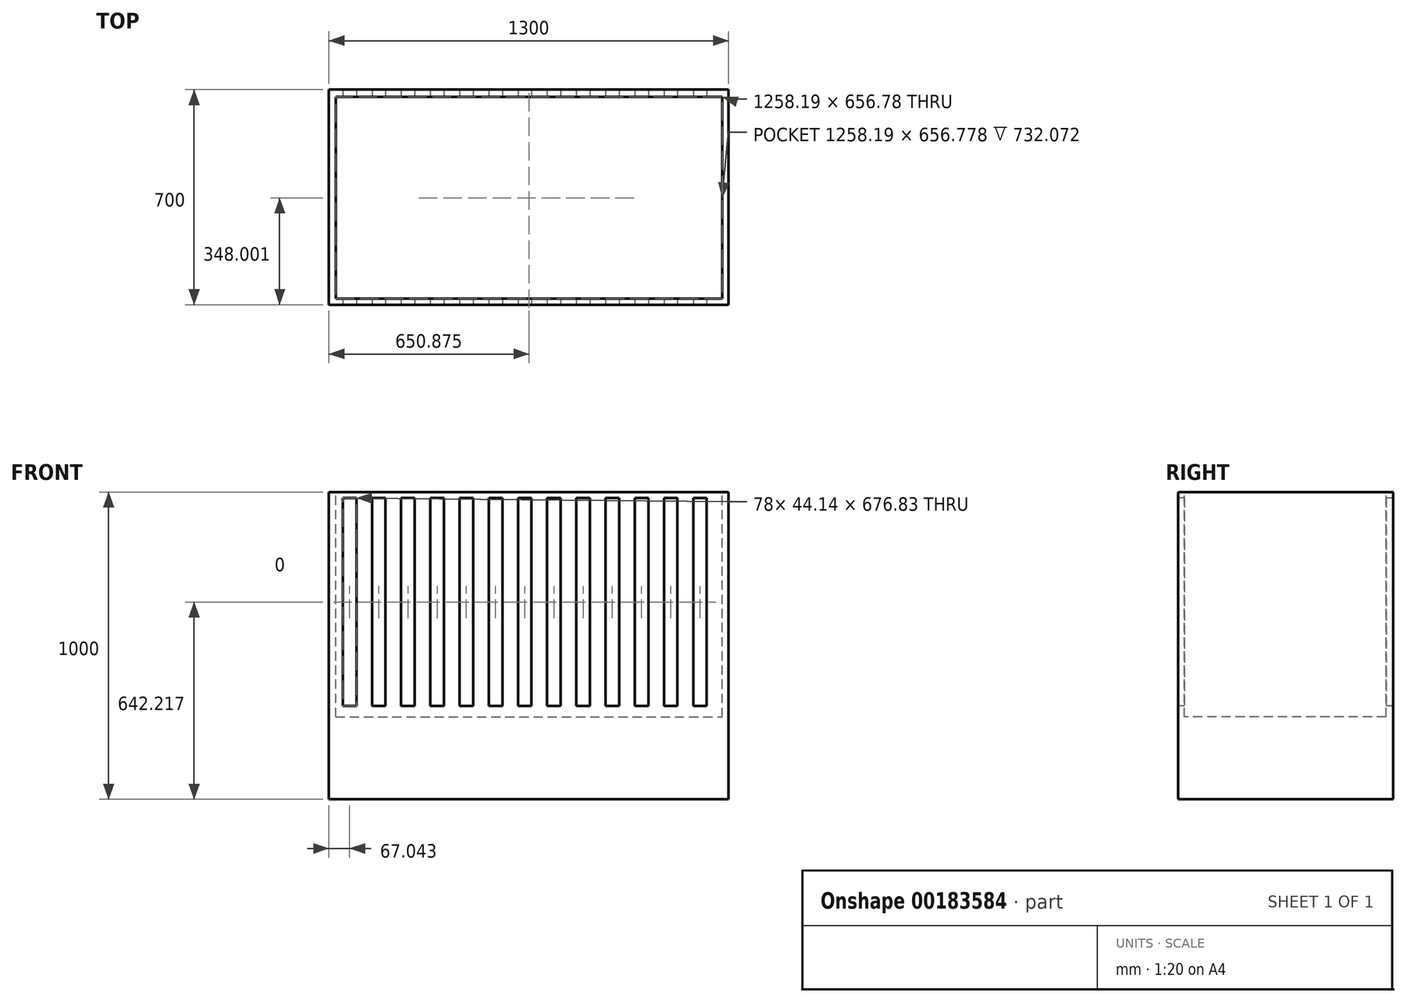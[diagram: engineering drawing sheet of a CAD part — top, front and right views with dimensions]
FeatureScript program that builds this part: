
annotation { "Feature Type Name" : "Feature", "Feature Type Description" : "" }
export const myFeature = defineFeature(function(context is Context, id is Id, definition is map)
    precondition{}
    {
        {
            var Q0;
            Q0=qCreatedBy(makeId("Top.planeOp"),FACE);
            var sketch = newSketch(context, id + "F0", { "sketchPlane" : qUnion([Q0])});
            skLineSegment(sketch, "E0.bottom", {"start": v(0, 0) * mm, "end": v(1300, 0) * mm});
            skLineSegment(sketch, "E0.top", {"start": v(0, 700) * mm, "end": v(1300, 700) * mm});
            skLineSegment(sketch, "E0.left", {"start": v(0, 0) * mm, "end": v(0, 700) * mm});
            skLineSegment(sketch, "E0.right", {"start": v(1300, 0) * mm, "end": v(1300, 700) * mm});
            skSolve(sketch);
        }
        {
            var Q0;
            Q0=makeQuery(id+"F0.imprint","IMPRINT",FACE,{"disambiguationData":[TD([[makeQuery(id+"F0.imprint","IMPRINT",EDGE,{"derivedFrom":sQuery(id+"F0.wireOp",EDGE,"E0.bottom")}),1.0]])]});
            extrude(context, id + "F1", {"entities" : qUnion([Q0]), "depth" : 1000 * mm});
        }
        {
            var Q0;
            Q0=makeQuery(id+"F1.opExtrude","CAP_FACE",FACE,{"disambiguationData":[OSD([sQuery(id+"F0.wireOp",EDGE,"E0.bottom"),sQuery(id+"F0.wireOp",EDGE,"E0.top"),sQuery(id+"F0.wireOp",EDGE,"E0.left"),sQuery(id+"F0.wireOp",EDGE,"E0.right")])],"isStart":false});
            var sketch = newSketch(context, id + "F2", { "sketchPlane" : qUnion([Q0])});
            skLineSegment(sketch, "E1.bottom", {"start": v(21.78, 676.4) * mm, "end": v(1279.97, 676.4) * mm});
            skLineSegment(sketch, "E1.top", {"start": v(21.78, 19.61) * mm, "end": v(1279.97, 19.61) * mm});
            skLineSegment(sketch, "E1.left", {"start": v(21.78, 676.4) * mm, "end": v(21.78, 19.61) * mm});
            skLineSegment(sketch, "E1.right", {"start": v(1279.97, 676.4) * mm, "end": v(1279.97, 19.61) * mm});
            skSolve(sketch);
        }
        {
            var Q0;
            Q0=makeQuery(id+"F2.imprint","IMPRINT",FACE,{"disambiguationData":[TD([[makeQuery(id+"F2.imprint","IMPRINT",EDGE,{"derivedFrom":sQuery(id+"F2.wireOp",EDGE,"E1.bottom")}),-1.0]])]});
            extrude(context, id + "F3", {"entities" : qUnion([Q0]), "operationType" : NewBodyOperationType.REMOVE, "oppositeDirection" : true, "depth" : 732.07 * mm});
        }
        {
            var Q0;
            Q0=makeQuery(id+"F1.opExtrude","SWEPT_FACE",FACE,{"disambiguationData":[OSD([sQuery(id+"F0.wireOp",EDGE,"E0.bottom")])]});
            var sketch = newSketch(context, id + "F4", { "sketchPlane" : qUnion([Q0])});
            skLineSegment(sketch, "E2.bottom", {"start": v(44.97, 980.63) * mm, "end": v(89.11, 980.63) * mm});
            skLineSegment(sketch, "E2.top", {"start": v(44.97, 303.8) * mm, "end": v(89.11, 303.8) * mm});
            skLineSegment(sketch, "E2.left", {"start": v(44.97, 980.63) * mm, "end": v(44.97, 303.8) * mm});
            skLineSegment(sketch, "E2.right", {"start": v(89.11, 980.63) * mm, "end": v(89.11, 303.8) * mm});
            skLineSegment(sketch, "E3.1.0.0", {"start": v(139.97, 980.63) * mm, "end": v(184.11, 980.63) * mm});
            skLineSegment(sketch, "E3.1.0.1", {"start": v(139.97, 980.63) * mm, "end": v(139.97, 303.8) * mm});
            skLineSegment(sketch, "E3.1.0.2", {"start": v(184.11, 980.63) * mm, "end": v(184.11, 303.8) * mm});
            skLineSegment(sketch, "E3.1.0.3", {"start": v(139.97, 303.8) * mm, "end": v(184.11, 303.8) * mm});
            skLineSegment(sketch, "E3.2.0.0", {"start": v(234.97, 980.63) * mm, "end": v(279.11, 980.63) * mm});
            skLineSegment(sketch, "E3.2.0.1", {"start": v(234.97, 980.63) * mm, "end": v(234.97, 303.8) * mm});
            skLineSegment(sketch, "E3.2.0.2", {"start": v(279.11, 980.63) * mm, "end": v(279.11, 303.8) * mm});
            skLineSegment(sketch, "E3.2.0.3", {"start": v(234.97, 303.8) * mm, "end": v(279.11, 303.8) * mm});
            skLineSegment(sketch, "E3.3.0.0", {"start": v(329.97, 980.63) * mm, "end": v(374.11, 980.63) * mm});
            skLineSegment(sketch, "E3.3.0.1", {"start": v(329.97, 980.63) * mm, "end": v(329.97, 303.8) * mm});
            skLineSegment(sketch, "E3.3.0.2", {"start": v(374.11, 980.63) * mm, "end": v(374.11, 303.8) * mm});
            skLineSegment(sketch, "E3.3.0.3", {"start": v(329.97, 303.8) * mm, "end": v(374.11, 303.8) * mm});
            skLineSegment(sketch, "E3.4.0.0", {"start": v(424.97, 980.63) * mm, "end": v(469.11, 980.63) * mm});
            skLineSegment(sketch, "E3.4.0.1", {"start": v(424.97, 980.63) * mm, "end": v(424.97, 303.8) * mm});
            skLineSegment(sketch, "E3.4.0.2", {"start": v(469.11, 980.63) * mm, "end": v(469.11, 303.8) * mm});
            skLineSegment(sketch, "E3.4.0.3", {"start": v(424.97, 303.8) * mm, "end": v(469.11, 303.8) * mm});
            skLineSegment(sketch, "E3.5.0.0", {"start": v(519.97, 980.63) * mm, "end": v(564.11, 980.63) * mm});
            skLineSegment(sketch, "E3.5.0.1", {"start": v(519.97, 980.63) * mm, "end": v(519.97, 303.8) * mm});
            skLineSegment(sketch, "E3.5.0.2", {"start": v(564.11, 980.63) * mm, "end": v(564.11, 303.8) * mm});
            skLineSegment(sketch, "E3.5.0.3", {"start": v(519.97, 303.8) * mm, "end": v(564.11, 303.8) * mm});
            skLineSegment(sketch, "E3.6.0.0", {"start": v(614.97, 980.63) * mm, "end": v(659.11, 980.63) * mm});
            skLineSegment(sketch, "E3.6.0.1", {"start": v(614.97, 980.63) * mm, "end": v(614.97, 303.8) * mm});
            skLineSegment(sketch, "E3.6.0.2", {"start": v(659.11, 980.63) * mm, "end": v(659.11, 303.8) * mm});
            skLineSegment(sketch, "E3.6.0.3", {"start": v(614.97, 303.8) * mm, "end": v(659.11, 303.8) * mm});
            skLineSegment(sketch, "E3.7.0.0", {"start": v(709.97, 980.63) * mm, "end": v(754.11, 980.63) * mm});
            skLineSegment(sketch, "E3.7.0.1", {"start": v(709.97, 980.63) * mm, "end": v(709.97, 303.8) * mm});
            skLineSegment(sketch, "E3.7.0.2", {"start": v(754.11, 980.63) * mm, "end": v(754.11, 303.8) * mm});
            skLineSegment(sketch, "E3.7.0.3", {"start": v(709.97, 303.8) * mm, "end": v(754.11, 303.8) * mm});
            skLineSegment(sketch, "E3.8.0.0", {"start": v(804.97, 980.63) * mm, "end": v(849.11, 980.63) * mm});
            skLineSegment(sketch, "E3.8.0.1", {"start": v(804.97, 980.63) * mm, "end": v(804.97, 303.8) * mm});
            skLineSegment(sketch, "E3.8.0.2", {"start": v(849.11, 980.63) * mm, "end": v(849.11, 303.8) * mm});
            skLineSegment(sketch, "E3.8.0.3", {"start": v(804.97, 303.8) * mm, "end": v(849.11, 303.8) * mm});
            skLineSegment(sketch, "E3.9.0.0", {"start": v(899.97, 980.63) * mm, "end": v(944.11, 980.63) * mm});
            skLineSegment(sketch, "E3.9.0.1", {"start": v(899.97, 980.63) * mm, "end": v(899.97, 303.8) * mm});
            skLineSegment(sketch, "E3.9.0.2", {"start": v(944.11, 980.63) * mm, "end": v(944.11, 303.8) * mm});
            skLineSegment(sketch, "E3.9.0.3", {"start": v(899.97, 303.8) * mm, "end": v(944.11, 303.8) * mm});
            skLineSegment(sketch, "E3.10.0.0", {"start": v(994.97, 980.63) * mm, "end": v(1039.11, 980.63) * mm});
            skLineSegment(sketch, "E3.10.0.1", {"start": v(994.97, 980.63) * mm, "end": v(994.97, 303.8) * mm});
            skLineSegment(sketch, "E3.10.0.2", {"start": v(1039.11, 980.63) * mm, "end": v(1039.11, 303.8) * mm});
            skLineSegment(sketch, "E3.10.0.3", {"start": v(994.97, 303.8) * mm, "end": v(1039.11, 303.8) * mm});
            skLineSegment(sketch, "E3.11.0.0", {"start": v(1089.97, 980.63) * mm, "end": v(1134.11, 980.63) * mm});
            skLineSegment(sketch, "E3.11.0.1", {"start": v(1089.97, 980.63) * mm, "end": v(1089.97, 303.8) * mm});
            skLineSegment(sketch, "E3.11.0.2", {"start": v(1134.11, 980.63) * mm, "end": v(1134.11, 303.8) * mm});
            skLineSegment(sketch, "E3.11.0.3", {"start": v(1089.97, 303.8) * mm, "end": v(1134.11, 303.8) * mm});
            skLineSegment(sketch, "E3.12.0.0", {"start": v(1184.97, 980.63) * mm, "end": v(1229.11, 980.63) * mm});
            skLineSegment(sketch, "E3.12.0.1", {"start": v(1184.97, 980.63) * mm, "end": v(1184.97, 303.8) * mm});
            skLineSegment(sketch, "E3.12.0.2", {"start": v(1229.11, 980.63) * mm, "end": v(1229.11, 303.8) * mm});
            skLineSegment(sketch, "E3.12.0.3", {"start": v(1184.97, 303.8) * mm, "end": v(1229.11, 303.8) * mm});
            skLineSegment(sketch, "E3.direction1", {"start": v(44.97, 980.63) * mm, "end": v(139.97, 980.63) * mm, "construction": true});
            skSolve(sketch);
        }
        {
            var Q0;
            Q0=makeQuery(id+"F4.imprint","IMPRINT",FACE,{"disambiguationData":[TD([[makeQuery(id+"F4.imprint","IMPRINT",EDGE,{"derivedFrom":sQuery(id+"F4.wireOp",EDGE,"E2.bottom")}),-1.0]])]});
            var Q1;
            Q1=makeQuery(id+"F4.imprint","IMPRINT",FACE,{"disambiguationData":[TD([[makeQuery(id+"F4.imprint","IMPRINT",EDGE,{"derivedFrom":sQuery(id+"F4.wireOp",EDGE,"E3.1.0.0")}),-1.0]])]});
            var Q2;
            Q2=makeQuery(id+"F4.imprint","IMPRINT",FACE,{"disambiguationData":[TD([[makeQuery(id+"F4.imprint","IMPRINT",EDGE,{"derivedFrom":sQuery(id+"F4.wireOp",EDGE,"E3.2.0.0")}),-1.0]])]});
            var Q3;
            Q3=makeQuery(id+"F4.imprint","IMPRINT",FACE,{"disambiguationData":[TD([[makeQuery(id+"F4.imprint","IMPRINT",EDGE,{"derivedFrom":sQuery(id+"F4.wireOp",EDGE,"E3.3.0.0")}),-1.0]])]});
            var Q4;
            Q4=makeQuery(id+"F4.imprint","IMPRINT",FACE,{"disambiguationData":[TD([[makeQuery(id+"F4.imprint","IMPRINT",EDGE,{"derivedFrom":sQuery(id+"F4.wireOp",EDGE,"E3.4.0.0")}),-1.0]])]});
            var Q5;
            Q5=makeQuery(id+"F4.imprint","IMPRINT",FACE,{"disambiguationData":[TD([[makeQuery(id+"F4.imprint","IMPRINT",EDGE,{"derivedFrom":sQuery(id+"F4.wireOp",EDGE,"E3.5.0.0")}),-1.0]])]});
            var Q6;
            Q6=makeQuery(id+"F4.imprint","IMPRINT",FACE,{"disambiguationData":[TD([[makeQuery(id+"F4.imprint","IMPRINT",EDGE,{"derivedFrom":sQuery(id+"F4.wireOp",EDGE,"E3.6.0.0")}),-1.0]])]});
            var Q7;
            Q7=makeQuery(id+"F4.imprint","IMPRINT",FACE,{"disambiguationData":[TD([[makeQuery(id+"F4.imprint","IMPRINT",EDGE,{"derivedFrom":sQuery(id+"F4.wireOp",EDGE,"E3.7.0.0")}),-1.0]])]});
            var Q8;
            Q8=makeQuery(id+"F4.imprint","IMPRINT",FACE,{"disambiguationData":[TD([[makeQuery(id+"F4.imprint","IMPRINT",EDGE,{"derivedFrom":sQuery(id+"F4.wireOp",EDGE,"E3.8.0.0")}),-1.0]])]});
            var Q9;
            Q9=makeQuery(id+"F4.imprint","IMPRINT",FACE,{"disambiguationData":[TD([[makeQuery(id+"F4.imprint","IMPRINT",EDGE,{"derivedFrom":sQuery(id+"F4.wireOp",EDGE,"E3.9.0.0")}),-1.0]])]});
            var Q10;
            Q10=makeQuery(id+"F4.imprint","IMPRINT",FACE,{"disambiguationData":[TD([[makeQuery(id+"F4.imprint","IMPRINT",EDGE,{"derivedFrom":sQuery(id+"F4.wireOp",EDGE,"E3.10.0.0")}),-1.0]])]});
            var Q11;
            Q11=makeQuery(id+"F4.imprint","IMPRINT",FACE,{"disambiguationData":[TD([[makeQuery(id+"F4.imprint","IMPRINT",EDGE,{"derivedFrom":sQuery(id+"F4.wireOp",EDGE,"E3.11.0.0")}),-1.0]])]});
            var Q12;
            Q12=makeQuery(id+"F4.imprint","IMPRINT",FACE,{"disambiguationData":[TD([[makeQuery(id+"F4.imprint","IMPRINT",EDGE,{"derivedFrom":sQuery(id+"F4.wireOp",EDGE,"E3.12.0.0")}),-1.0]])]});
            extrude(context, id + "F5", {"entities" : qUnion([Q0, Q1, Q2, Q3, Q4, Q5, Q6, Q7, Q8, Q9, Q10, Q11, Q12]), "operationType" : NewBodyOperationType.REMOVE, "oppositeDirection" : true, "depth" : 781.75 * mm});
        }
    });
